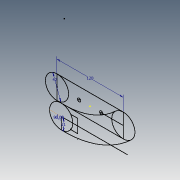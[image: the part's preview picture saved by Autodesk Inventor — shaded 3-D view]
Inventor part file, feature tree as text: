
AUTODESK INVENTOR PART (.ipt)
format: ipt  version: 2013 (Build 170138000, 138)  size: 69,120 bytes
history: native  units: mm
features: sketch x2
ambient origin geometry x8: Origin, YZ Plane, XZ Plane, XY Plane, X Axis, Y Axis, Z Axis, Center Point
feature tree (2):
  sketch  "Sketch1"  dims[d27=120.0mm]
  sketch  "Sketch2"  dims[d29=42.0mm d55=21.0mm d56=90.0deg]
